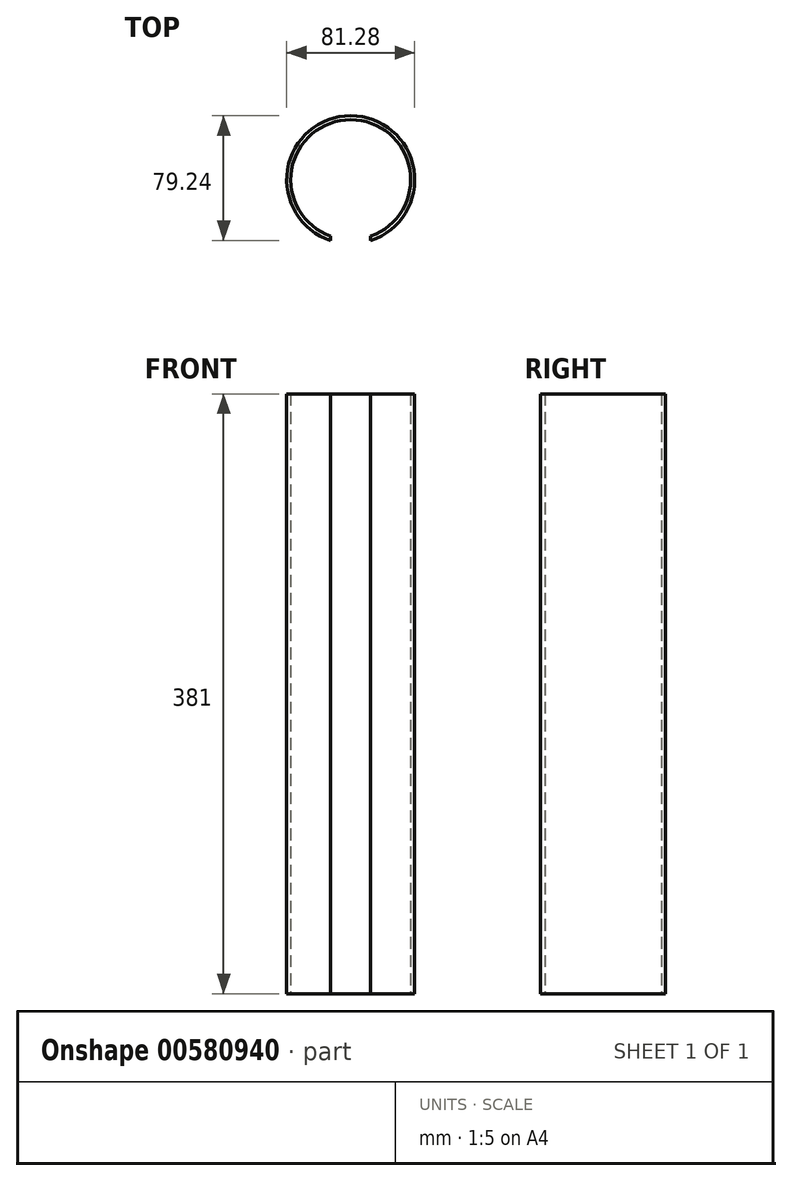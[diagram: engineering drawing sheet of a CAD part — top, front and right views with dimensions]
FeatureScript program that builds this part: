
annotation { "Feature Type Name" : "Feature", "Feature Type Description" : "" }
export const myFeature = defineFeature(function(context is Context, id is Id, definition is map)
    precondition{}
    {
        {
            var Q0;
            Q0=qCreatedBy(makeId("Top.planeOp"),FACE);
            var sketch = newSketch(context, id + "F0", { "sketchPlane" : qUnion([Q0])});
            skArc(sketch, "E0", {"start": v(12.7, -35.92) * mm, "mid": v(0, 38.1) * mm, "end": v(-12.7, -35.92) * mm});
            skArc(sketch, "E1", {"start": v(12.7, -38.6) * mm, "mid": v(0, 40.64) * mm, "end": v(-12.7, -38.6) * mm});
            skLineSegment(sketch, "E2", {"start": v(-12.7, -35.92) * mm, "end": v(-12.7, -38.6) * mm});
            skLineSegment(sketch, "E3", {"start": v(12.7, -35.92) * mm, "end": v(12.7, -38.6) * mm});
            skSolve(sketch);
        }
        {
            var Q0;
            Q0=makeQuery(id+"F0.imprint","IMPRINT",FACE,{"disambiguationData":[TD([[makeQuery(id+"F0.imprint","IMPRINT",EDGE,{"derivedFrom":sQuery(id+"F0.wireOp",EDGE,"E0")}),-1.0]])]});
            extrude(context, id + "F1", {"entities" : qUnion([Q0]), "depth" : 381 * mm, "offsetDistance" : 25.4 * mm});
        }
    });
